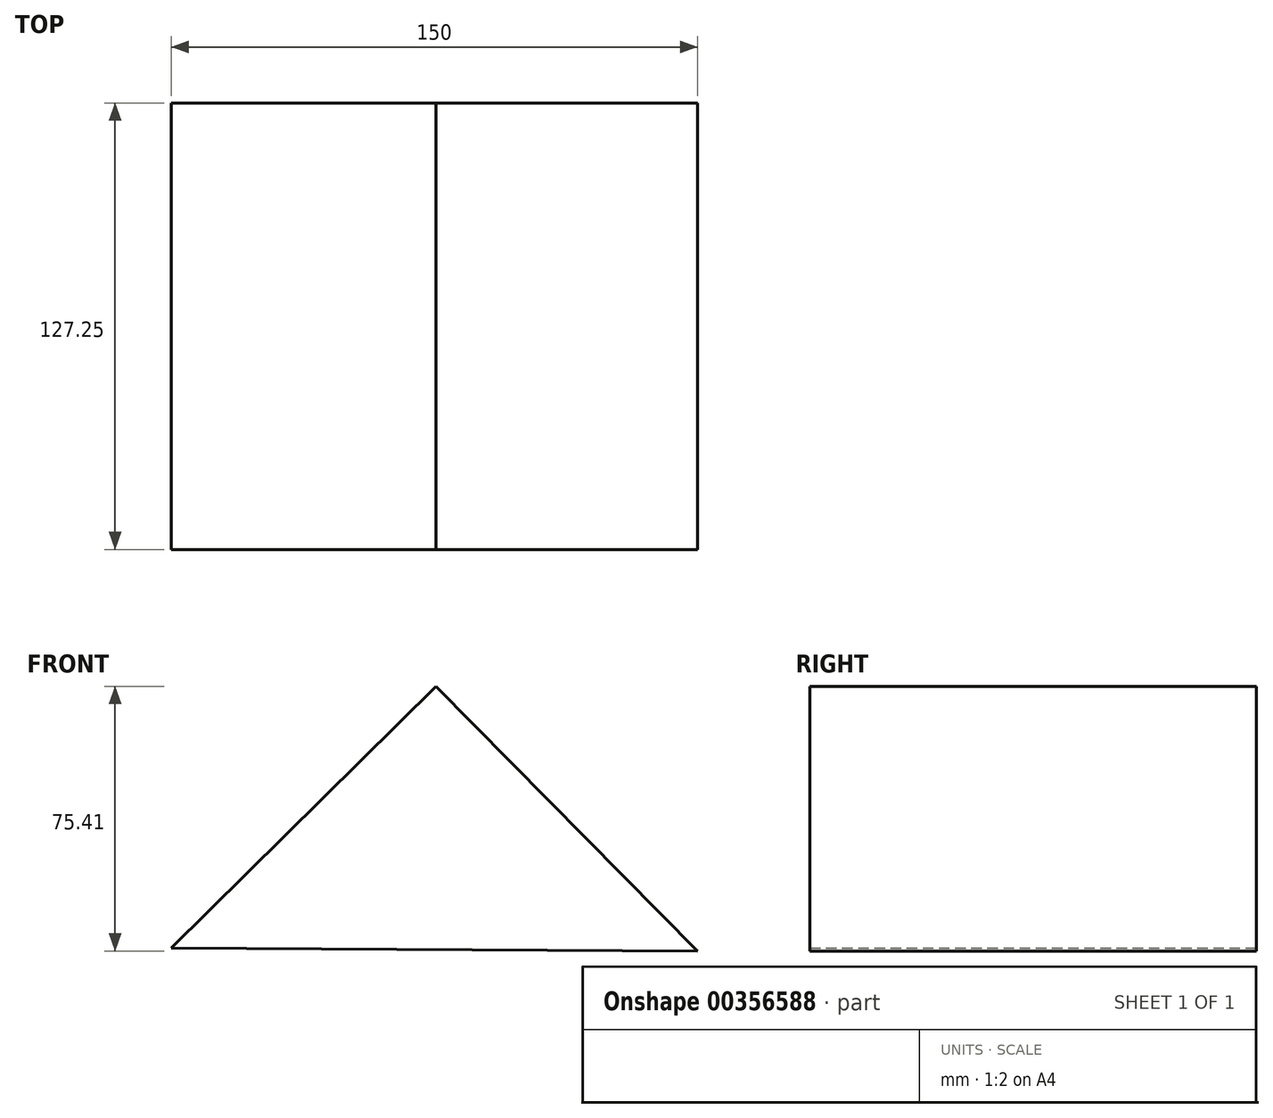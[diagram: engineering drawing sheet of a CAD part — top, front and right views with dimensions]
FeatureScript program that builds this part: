
annotation { "Feature Type Name" : "Feature", "Feature Type Description" : "" }
export const myFeature = defineFeature(function(context is Context, id is Id, definition is map)
    precondition{}
    {
        {
            var Q0;
            Q0=qCreatedBy(makeId("Front.planeOp"),FACE);
            var sketch = newSketch(context, id + "F0", { "sketchPlane" : qUnion([Q0])});
            skLineSegment(sketch, "E0", {"start": v(-120.02, -49.9) * mm, "end": v(-44.54, 24.67) * mm});
            skLineSegment(sketch, "E1", {"start": v(-44.54, 24.67) * mm, "end": v(29.98, -50.74) * mm});
            skLineSegment(sketch, "E2", {"start": v(29.98, -50.74) * mm, "end": v(-120.02, -49.9) * mm});
            skSolve(sketch);
        }
        {
            var Q0;
            Q0 = qSketchRegion(id + "F0", true);
            extrude(context, id + "F1", {"entities" : qUnion([Q0]), "depth" : 127.25 * mm});
        }
    });
